# Revit family: basic_set_for_exafill_s_bath_filler_finish_set_with_waste_overflow_set_58116180____
name_source: partatom
category: Plumbing Fixtures
revit_build: Autodesk Revit 2015 (Build: 20140903_1530(x64)
units: mm (PartAtom-declared; Revit-internal decimal feet)

## types (1)
- Chrome 000
    BIMobject category = Drainage
    BOSUseNativeGeometries = 1
    Brand url = http://www.hansgrohe-int.com
    Date of publishing = 1/12/2016
    Default Elevation = 4' - 0"
    Design country = Germany
    EAN code = https://4011097433110
    Edition number = 1
    IFC Classification = Sanitary Terminal
    Installation instructions = https://pro.hansgrohe-int.com
    Manufacturer country = Germany
    Manufacturer name = Hansgrohe
    Masterformat 2014 Code = 22 13 16
    Masterformat 2014 Description = Sanitary Waste and Vent Piping
    Material main = Chrome
    NBS Reference Code = 31-76
    NBS Reference Description = Sanitary Dispensing And Disposal Units
    Nominal height = 0
    Nominal width = 0
    OmniClass Code = 23-21 23 27
    OmniClass Description = Residential Waste Disposal Units
    Product Guid = 7b2c0ab1-d1ef-45c6-a7f9-186a76998136
    Product SKU = 58116180
    Product data url = https://bimobject.com
    Product family = Waste systems
    Product group = Basic set for bath filler with waste and overflow
    Product url = https://pro.hansgrohe-int.com
    QR code = http://bimobject.com
    Technical description = https://pro.hansgrohe-int.com
    UNSPSC Code = 301815
    Uniclass 1.4 Code = L7218
    Uniclass 1.4 Description = Sanitary disposal units
    Uniclass 2.0 Code = PR-31-76
    Uniclass 2.0 Description = Sanitary Dispensing And Disposal Units
    Uniclass 2015 Code = Pr_60_45_90
    Uniclass 2015 Name = Wastewater and water mixer products
    Uniformat II Code = D2010
    Uniformat II Description = Plumbing Fixtures
    Weight Net (Kg) = 0

## geometry (parser evidence)
native form markers: Sweep x1
no freeform markers — native parametric forms only
